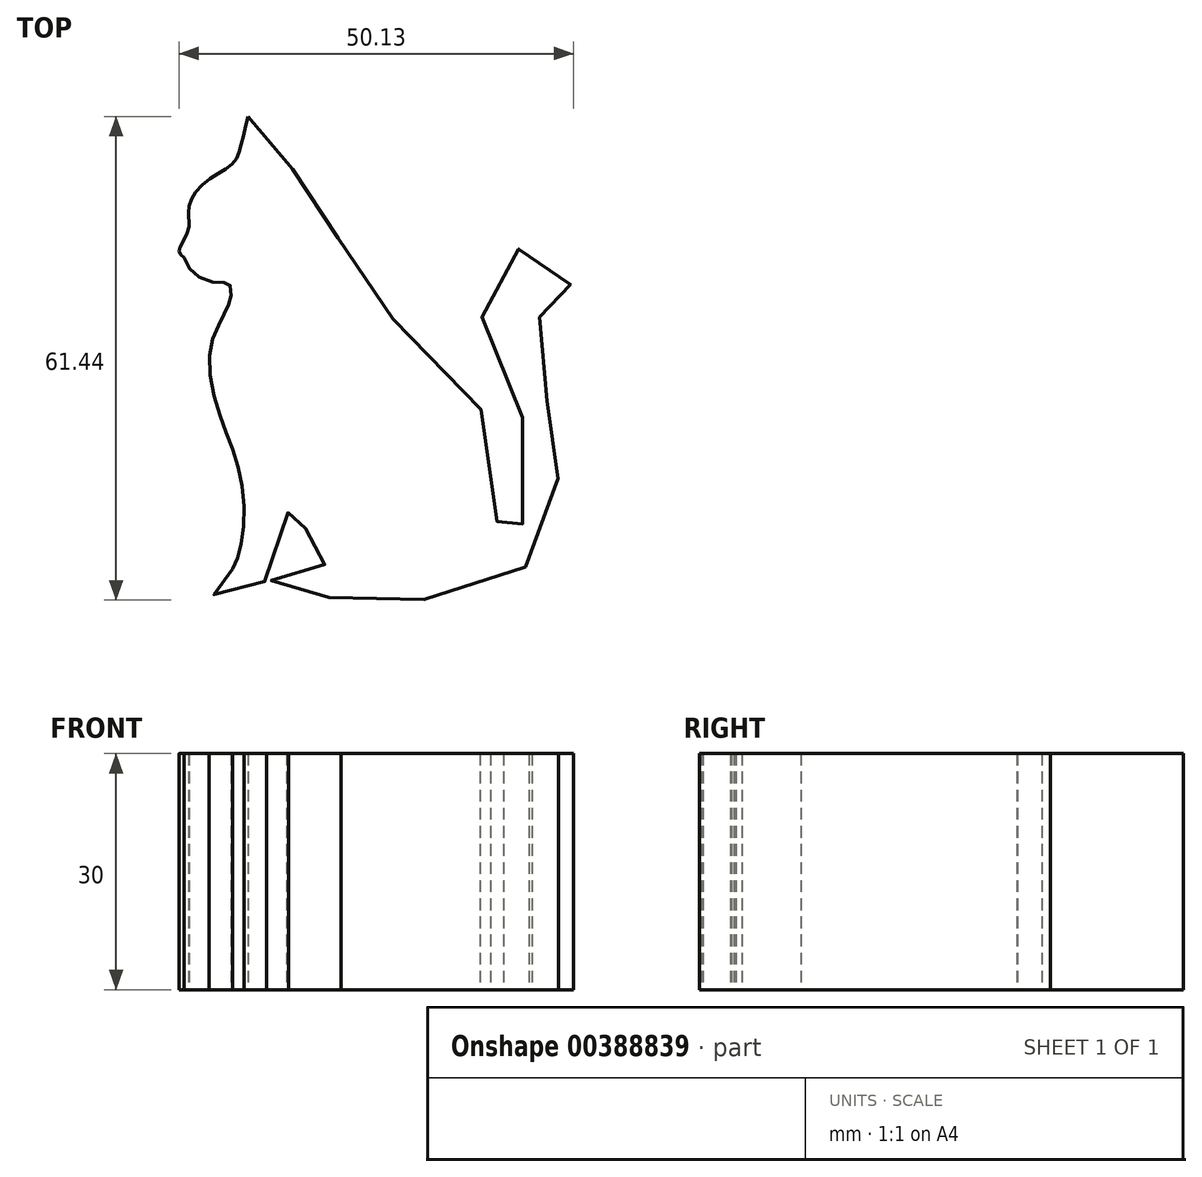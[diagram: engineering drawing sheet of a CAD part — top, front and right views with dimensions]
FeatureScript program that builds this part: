
annotation { "Feature Type Name" : "Feature", "Feature Type Description" : "" }
export const myFeature = defineFeature(function(context is Context, id is Id, definition is map)
    precondition{}
    {
        {
            var Q0;
            Q0=qCreatedBy(makeId("Top.planeOp"),FACE);
            var sketch = newSketch(context, id + "F0", { "sketchPlane" : qUnion([Q0])});
            skFitSpline(sketch, "E0", {"points": [v(-14.37, 28.96) * mm, v(-15.28, 25.1) * mm, v(-16.19, 23.05) * mm, v(-18.91, 21.24) * mm, v(-21.5, 18.55) * mm, v(-21.9, 16.63) * mm, v(-21.87, 15.78) * mm, v(-21.92, 14.52) * mm, v(-23.06, 12.25) * mm, v(-23.06, 11.62) * mm, v(-22.5, 11) * mm], "startDerivative": vector(-6.62, -29.03) * mm, "endDerivative": vector(10.4, -9.58) * mm});
            skFitSpline(sketch, "E1", {"points": [v(-22.5, 11) * mm, v(-21.06, 8.88) * mm, v(-18.01, 7.83) * mm, v(-16.81, 7.75) * mm, v(-16.49, 6.3) * mm, v(-16.9, 4.86) * mm, v(-17.93, 2.78) * mm, v(-19.22, -1) * mm, v(-18.26, -8.06) * mm, v(-16.25, -13.44) * mm, v(-14.88, -19.87) * mm, v(-15.32, -25.88) * mm, v(-16.29, -28.52) * mm], "startDerivative": vector(14.4, -32.29) * mm, "endDerivative": vector(-13.87, -31.03) * mm});
            skFitSpline(sketch, "E2", {"points": [v(-16.29, -28.52) * mm, v(-17.22, -28.52) * mm, v(-18.3, -28.52) * mm, v(-19.26, -30.3) * mm, v(-18.75, -31.77) * mm, v(-15.74, -32.06) * mm, v(-13.47, -31.94) * mm, v(-12.28, -30.3) * mm, v(-11.37, -26.9) * mm, v(-9.78, -23.2) * mm, v(-9.27, -20.03) * mm, v(-9.44, -19.57) * mm, v(-8.59, -20.42) * mm, v(-7.4, -22.75) * mm, v(-5.24, -25.59) * mm, v(-2.57, -27.97) * mm, v(-4.84, -27.97) * mm, v(-8.08, -27.91) * mm, v(-10, -28.52) * mm, v(-11.48, -30.13) * mm, v(-11.88, -31.66) * mm, v(-7.23, -32.11) * mm, v(-1.32, -32.23) * mm, v(3.1, -32.17) * mm, v(16.31, -31.99) * mm, v(20.7, -28.52) * mm, v(23.95, -22.35) * mm, v(25.05, -16.24) * mm, v(24.68, -10.4) * mm, v(24.15, -8.72) * mm, v(21.47, 0) * mm, v(21.86, 3) * mm, v(24.34, 3.82) * mm, v(26.48, 4.58) * mm, v(26.96, 6.68) * mm, v(26.1, 8.3) * mm, v(23.86, 10.83) * mm, v(20.9, 12.03) * mm, v(17.99, 11.55) * mm, v(15.17, 6.3) * mm, v(17.04, -1.2) * mm, v(20.47, -9.16) * mm, v(21.71, -16.13) * mm, v(19.23, -25.3) * mm, v(16.65, -27.01) * mm, v(17.6, -20.9) * mm, v(17.13, -11.55) * mm, v(10.07, -2.58) * mm, v(2.43, 4.87) * mm, v(-2.15, 10.7) * mm, v(-3.4, 15.84) * mm, v(-5.87, 20.24) * mm, v(-9.79, 23.39) * mm, v(-10.17, 26.06) * mm, v(-14.37, 28.96) * mm], "startDerivative": vector(-101.75, -7.68) * mm, "endDerivative": vector(-267.97, 125.3) * mm});
            skFitSpline(sketch, "E3", {"points": [v(-7.6, -0.76) * mm, v(-7.4, -0.95) * mm], "startDerivative": vector(0.2, -0.2) * mm, "endDerivative": vector(0.2, -0.2) * mm});
            skSolve(sketch);
        }
        {
            var Q0;
            Q0=makeQuery(id+"F0.imprint","IMPRINT",FACE,{"disambiguationData":[TD([[makeQuery(id+"F0.imprint","IMPRINT",EDGE,{"derivedFrom":sQuery(id+"F0.wireOp",EDGE,"E0")}),1.0]])]});
            extrude(context, id + "F1", {"entities" : qUnion([Q0]), "depth" : 30 * mm});
        }
    });
